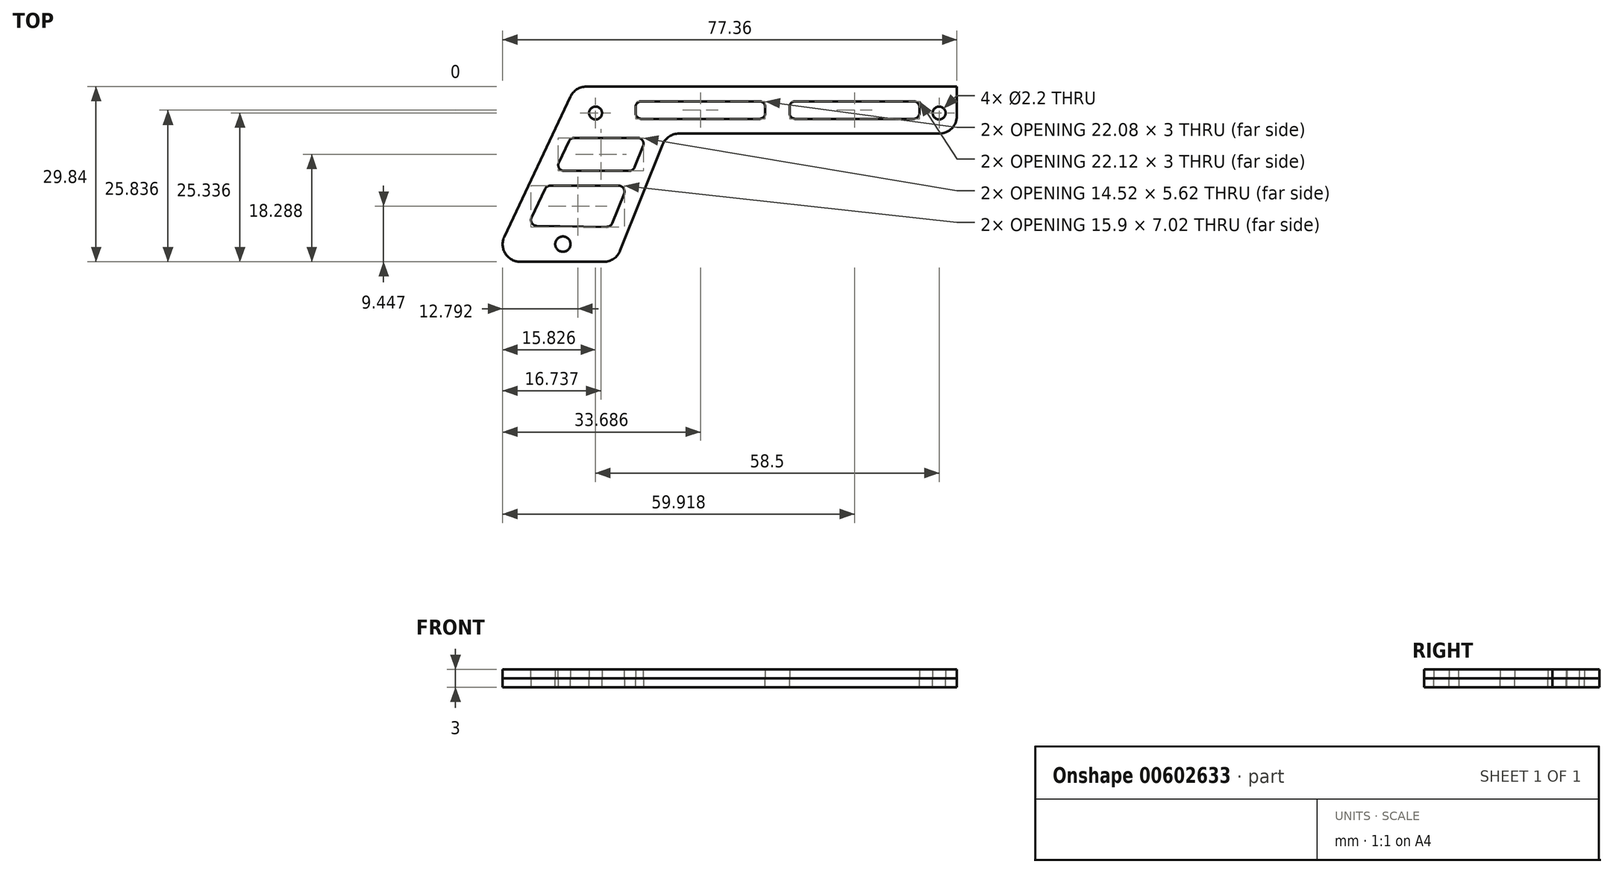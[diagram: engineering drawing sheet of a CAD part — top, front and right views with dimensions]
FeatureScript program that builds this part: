
annotation { "Feature Type Name" : "Feature", "Feature Type Description" : "" }
export const myFeature = defineFeature(function(context is Context, id is Id, definition is map)
    precondition{}
    {
        {
            var Q0;
            Q0=qCreatedBy(makeId("Top.planeOp"),FACE);
            var sketch = newSketch(context, id + "F0", { "sketchPlane" : qUnion([Q0])});
            skLineSegment(sketch, "E0", {"start": v(-37.68, 30.53) * mm, "end": v(27.32, 30.53) * mm});
            skLineSegment(sketch, "E1", {"start": v(27.32, 30.53) * mm, "end": v(27.32, 22.53) * mm});
            skLineSegment(sketch, "E2", {"start": v(27.32, 22.53) * mm, "end": v(-22.03, 22.53) * mm});
            skLineSegment(sketch, "E3", {"start": v(-22.03, 22.53) * mm, "end": v(-30.77, 0.69) * mm});
            skLineSegment(sketch, "E4", {"start": v(-30.77, 0.69) * mm, "end": v(-51.77, 0.69) * mm});
            skLineSegment(sketch, "E5", {"start": v(-51.77, 0.69) * mm, "end": v(-37.68, 30.53) * mm});
            skPoint(sketch, "E6", {"position": v(24.29, 26.03) * mm});
            skPoint(sketch, "E7", {"position": v(-34.21, 26.03) * mm});
            skCircle(sketch, "E8", {"center": v(-34.21, 26.03) * mm, "radius": 1.1 * mm});
            skCircle(sketch, "E9", {"center": v(24.29, 26.03) * mm, "radius": 1.1 * mm});
            skCircle(sketch, "E10", {"center": v(-39.77, 3.69) * mm, "radius": 1.3 * mm});
            skLineSegment(sketch, "E11", {"start": v(-45.77, 6.83) * mm, "end": v(-42.54, 13.65) * mm});
            skLineSegment(sketch, "E12", {"start": v(-42.54, 13.65) * mm, "end": v(-28.82, 13.65) * mm});
            skLineSegment(sketch, "E13", {"start": v(-28.82, 13.65) * mm, "end": v(-31.63, 6.62) * mm});
            skLineSegment(sketch, "E14", {"start": v(-31.63, 6.62) * mm, "end": v(-45.77, 6.83) * mm});
            skLineSegment(sketch, "E15", {"start": v(-41.14, 16.17) * mm, "end": v(-38.49, 21.8) * mm});
            skLineSegment(sketch, "E16", {"start": v(-38.49, 21.8) * mm, "end": v(-25.56, 21.8) * mm});
            skLineSegment(sketch, "E17", {"start": v(-25.56, 21.8) * mm, "end": v(-27.8, 16.17) * mm});
            skLineSegment(sketch, "E18", {"start": v(-27.8, 16.17) * mm, "end": v(-41.14, 16.17) * mm});
            skLineSegment(sketch, "E19", {"start": v(27.32, 26.53) * mm, "end": v(-39.57, 26.53) * mm, "construction": true});
            skLineSegment(sketch, "E20.bottom", {"start": v(20.94, 28.03) * mm, "end": v(-1.18, 28.03) * mm});
            skLineSegment(sketch, "E20.top", {"start": v(20.94, 25.03) * mm, "end": v(-1.18, 25.03) * mm});
            skLineSegment(sketch, "E20.left", {"start": v(20.94, 28.03) * mm, "end": v(20.94, 25.03) * mm});
            skLineSegment(sketch, "E20.right", {"start": v(-1.18, 28.03) * mm, "end": v(-1.18, 25.03) * mm});
            skLineSegment(sketch, "E21.bottom", {"start": v(-5.32, 28.03) * mm, "end": v(-27.4, 28.03) * mm});
            skLineSegment(sketch, "E21.top", {"start": v(-5.32, 25.03) * mm, "end": v(-27.4, 25.03) * mm});
            skLineSegment(sketch, "E21.left", {"start": v(-5.32, 28.03) * mm, "end": v(-5.32, 25.03) * mm});
            skLineSegment(sketch, "E21.right", {"start": v(-27.4, 28.03) * mm, "end": v(-27.4, 25.03) * mm});
            skSolve(sketch);
        }
        {
            var Q0;
            Q0=makeQuery(id+"F0.imprint","IMPRINT",FACE,{"disambiguationData":[TD([[makeQuery(id+"F0.imprint","IMPRINT",EDGE,{"derivedFrom":sQuery(id+"F0.wireOp",EDGE,"E0")}),-1.0]])]});
            extrude(context, id + "F1", {"entities" : qUnion([Q0]), "depth" : 1.5 * mm, "offsetDistance" : 25 * mm});
        }
        {
            var Q0;
            Q0=makeQuery(id+"F1.opExtrude","SWEPT_EDGE",EDGE,{"disambiguationData":[OSD([sQuery(id+"F0.wireOp",EDGE,"E2"),sQuery(id+"F0.wireOp",EDGE,"E3")])]});
            var Q1;
            Q1=makeQuery(id+"F1.opExtrude","SWEPT_EDGE",EDGE,{"disambiguationData":[OSD([sQuery(id+"F0.wireOp",EDGE,"E0"),sQuery(id+"F0.wireOp",EDGE,"E5")])]});
            var Q2;
            Q2=makeQuery(id+"F1.opExtrude","SWEPT_EDGE",EDGE,{"disambiguationData":[OSD([sQuery(id+"F0.wireOp",EDGE,"E4"),sQuery(id+"F0.wireOp",EDGE,"E5")])]});
            var Q3;
            Q3=makeQuery(id+"F1.opExtrude","SWEPT_EDGE",EDGE,{"disambiguationData":[OSD([sQuery(id+"F0.wireOp",EDGE,"E3"),sQuery(id+"F0.wireOp",EDGE,"E4")])]});
            var Q4;
            Q4=makeQuery(id+"F1.opExtrude","SWEPT_EDGE",EDGE,{"disambiguationData":[OSD([sQuery(id+"F0.wireOp",EDGE,"E1"),sQuery(id+"F0.wireOp",EDGE,"E2")])]});
            fillet(context, id + "F2", {"entities" : qUnion([Q0, Q1, Q2, Q3, Q4]), "radius" : 3 * mm, "tangentPropagation" : true, "allowEdgeOverflow" : false});
        }
        {
            var Q0;
            Q0=makeQuery(id+"F1.opExtrude","SWEPT_EDGE",EDGE,{"disambiguationData":[OSD([sQuery(id+"F0.wireOp",EDGE,"E11"),sQuery(id+"F0.wireOp",EDGE,"E14")])]});
            var Q1;
            Q1=makeQuery(id+"F1.opExtrude","SWEPT_EDGE",EDGE,{"disambiguationData":[OSD([sQuery(id+"F0.wireOp",EDGE,"E11"),sQuery(id+"F0.wireOp",EDGE,"E12")])]});
            var Q2;
            Q2=makeQuery(id+"F1.opExtrude","SWEPT_EDGE",EDGE,{"disambiguationData":[OSD([sQuery(id+"F0.wireOp",EDGE,"E12"),sQuery(id+"F0.wireOp",EDGE,"E13")])]});
            var Q3;
            Q3=makeQuery(id+"F1.opExtrude","SWEPT_EDGE",EDGE,{"disambiguationData":[OSD([sQuery(id+"F0.wireOp",EDGE,"E13"),sQuery(id+"F0.wireOp",EDGE,"E14")])]});
            var Q4;
            Q4=makeQuery(id+"F1.opExtrude","SWEPT_EDGE",EDGE,{"disambiguationData":[OSD([sQuery(id+"F0.wireOp",EDGE,"E17"),sQuery(id+"F0.wireOp",EDGE,"E18")])]});
            var Q5;
            Q5=makeQuery(id+"F1.opExtrude","SWEPT_EDGE",EDGE,{"disambiguationData":[OSD([sQuery(id+"F0.wireOp",EDGE,"E16"),sQuery(id+"F0.wireOp",EDGE,"E17")])]});
            var Q6;
            Q6=makeQuery(id+"F1.opExtrude","SWEPT_EDGE",EDGE,{"disambiguationData":[OSD([sQuery(id+"F0.wireOp",EDGE,"E15"),sQuery(id+"F0.wireOp",EDGE,"E16")])]});
            var Q7;
            Q7=makeQuery(id+"F1.opExtrude","SWEPT_EDGE",EDGE,{"disambiguationData":[OSD([sQuery(id+"F0.wireOp",EDGE,"E15"),sQuery(id+"F0.wireOp",EDGE,"E18")])]});
            var Q8;
            Q8=makeQuery(id+"F1.opExtrude","SWEPT_EDGE",EDGE,{"disambiguationData":[OSD([sQuery(id+"F0.wireOp",EDGE,"E21.top"),sQuery(id+"F0.wireOp",EDGE,"E21.right")])]});
            var Q9;
            Q9=makeQuery(id+"F1.opExtrude","SWEPT_EDGE",EDGE,{"disambiguationData":[OSD([sQuery(id+"F0.wireOp",EDGE,"E21.bottom"),sQuery(id+"F0.wireOp",EDGE,"E21.right")])]});
            var Q10;
            Q10=makeQuery(id+"F1.opExtrude","SWEPT_EDGE",EDGE,{"disambiguationData":[OSD([sQuery(id+"F0.wireOp",EDGE,"E21.bottom"),sQuery(id+"F0.wireOp",EDGE,"E21.left")])]});
            var Q11;
            Q11=makeQuery(id+"F1.opExtrude","SWEPT_EDGE",EDGE,{"disambiguationData":[OSD([sQuery(id+"F0.wireOp",EDGE,"E21.top"),sQuery(id+"F0.wireOp",EDGE,"E21.left")])]});
            var Q12;
            Q12=makeQuery(id+"F1.opExtrude","SWEPT_EDGE",EDGE,{"disambiguationData":[OSD([sQuery(id+"F0.wireOp",EDGE,"E20.top"),sQuery(id+"F0.wireOp",EDGE,"E20.left")])]});
            var Q13;
            Q13=makeQuery(id+"F1.opExtrude","SWEPT_EDGE",EDGE,{"disambiguationData":[OSD([sQuery(id+"F0.wireOp",EDGE,"E20.bottom"),sQuery(id+"F0.wireOp",EDGE,"E20.left")])]});
            var Q14;
            Q14=makeQuery(id+"F1.opExtrude","SWEPT_EDGE",EDGE,{"disambiguationData":[OSD([sQuery(id+"F0.wireOp",EDGE,"E20.top"),sQuery(id+"F0.wireOp",EDGE,"E20.right")])]});
            var Q15;
            Q15=makeQuery(id+"F1.opExtrude","SWEPT_EDGE",EDGE,{"disambiguationData":[OSD([sQuery(id+"F0.wireOp",EDGE,"E20.bottom"),sQuery(id+"F0.wireOp",EDGE,"E20.right")])]});
            fillet(context, id + "F3", {"entities" : qUnion([Q0, Q1, Q2, Q3, Q4, Q5, Q6, Q7, Q8, Q9, Q10, Q11, Q12, Q13, Q14, Q15]), "radius" : 1 * mm, "tangentPropagation" : true, "allowEdgeOverflow" : false});
        }
        {
            var Q0;
            Q0=makeQuery(id+"F1.opExtrude","SWEPT_BODY",BODY,{"disambiguationData":[OSD([sQuery(id+"F0.wireOp",EDGE,"E0"),sQuery(id+"F0.wireOp",EDGE,"E1"),sQuery(id+"F0.wireOp",EDGE,"E2"),sQuery(id+"F0.wireOp",EDGE,"E3"),sQuery(id+"F0.wireOp",EDGE,"E4"),sQuery(id+"F0.wireOp",EDGE,"E5"),sQuery(id+"F0.wireOp",EDGE,"E8"),sQuery(id+"F0.wireOp",EDGE,"E9"),sQuery(id+"F0.wireOp",EDGE,"E10"),sQuery(id+"F0.wireOp",EDGE,"E11"),sQuery(id+"F0.wireOp",EDGE,"E12"),sQuery(id+"F0.wireOp",EDGE,"E13"),sQuery(id+"F0.wireOp",EDGE,"E14"),sQuery(id+"F0.wireOp",EDGE,"E15"),sQuery(id+"F0.wireOp",EDGE,"E16"),sQuery(id+"F0.wireOp",EDGE,"E17"),sQuery(id+"F0.wireOp",EDGE,"E18"),sQuery(id+"F0.wireOp",EDGE,"E20.bottom"),sQuery(id+"F0.wireOp",EDGE,"E20.top"),sQuery(id+"F0.wireOp",EDGE,"E20.left"),sQuery(id+"F0.wireOp",EDGE,"E20.right"),sQuery(id+"F0.wireOp",EDGE,"E21.bottom"),sQuery(id+"F0.wireOp",EDGE,"E21.top"),sQuery(id+"F0.wireOp",EDGE,"E21.left"),sQuery(id+"F0.wireOp",EDGE,"E21.right")])]});
            var Q1;
            Q1=qCreatedBy(makeId("Top.planeOp"),FACE);
            mirror(context, id + "F4", {"entities" : qUnion([Q0]), "mirrorPlane" : qUnion([Q1])});
        }
    });
